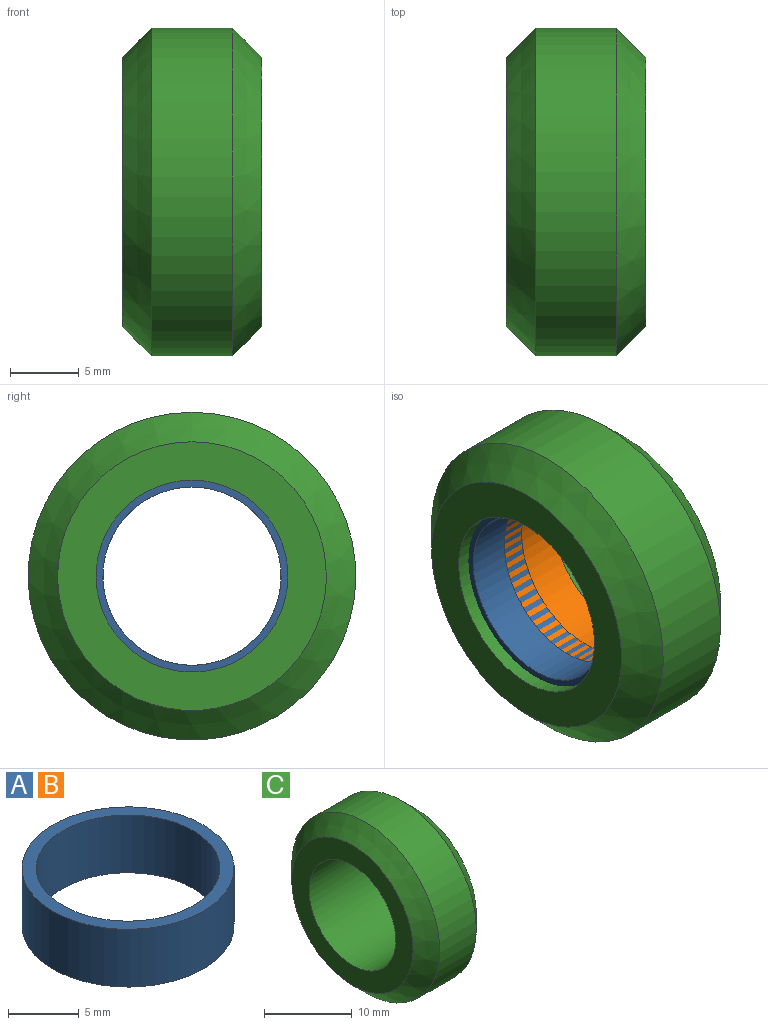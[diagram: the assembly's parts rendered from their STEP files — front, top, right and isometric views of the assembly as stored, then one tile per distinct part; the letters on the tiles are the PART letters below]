
ASSEMBLY  parts=3 mates=2
PART A: 4 faces, bbox 15x15x5 mm
  f0: plane 15x15mm, normal (0,0,-1), area 44mm2, adj f2,f3
  f1: plane 15x15mm, normal (0,0,1), area 44mm2, adj f2,f3
  f2: cylinder r=7.5mm len=15mm, axis (0,0,1), area 235.6mm2, adj f0,f1
  f3: cylinder r=6.5mm len=13mm, axis (0,0,1), area 204.2mm2, adj f0,f1
PART B: same geometry as A
PART C: 6 faces, bbox 10.2x23.9x23.9 mm
  f0: plane 19.6x19.6mm, normal (1,0,0), area 147.8mm2, adj f1,f5
  f1: cone r=11.95mm half-angle=45deg, axis (-1,0,0), area 207.8mm2, adj f0,f2
  f2: cylinder r=11.95mm len=23.9mm, axis (-1,0,0), area 443mm2, adj f1,f3
  f3: cone r=9.8mm half-angle=45deg, axis (1,0,0), area 207.8mm2, adj f2,f4
  f4: plane 19.6x19.6mm, normal (-1,0,0), area 147.8mm2, adj f3,f5
  f5: cylinder r=7mm len=14mm, axis (-1,0,0), area 448.6mm2, adj f0,f4
PLACE A rot(axis=(0,-1,0),90deg) t=(-10.54,-5.68,1.39)mm
PLACE B rot(axis=(0,1,0),90deg) t=(-12.34,-5.68,1.39)mm
PLACE C t=(-11.44,-5.68,1.39)mm
MATE fastened A.f2 <-> C.f5  axis (-1,0,0) through (-15.54,-5.68,1.39)mm
MATE fastened B.f2 <-> C.f5  axis (-1,0,0) through (-7.34,-5.68,1.39)mm
